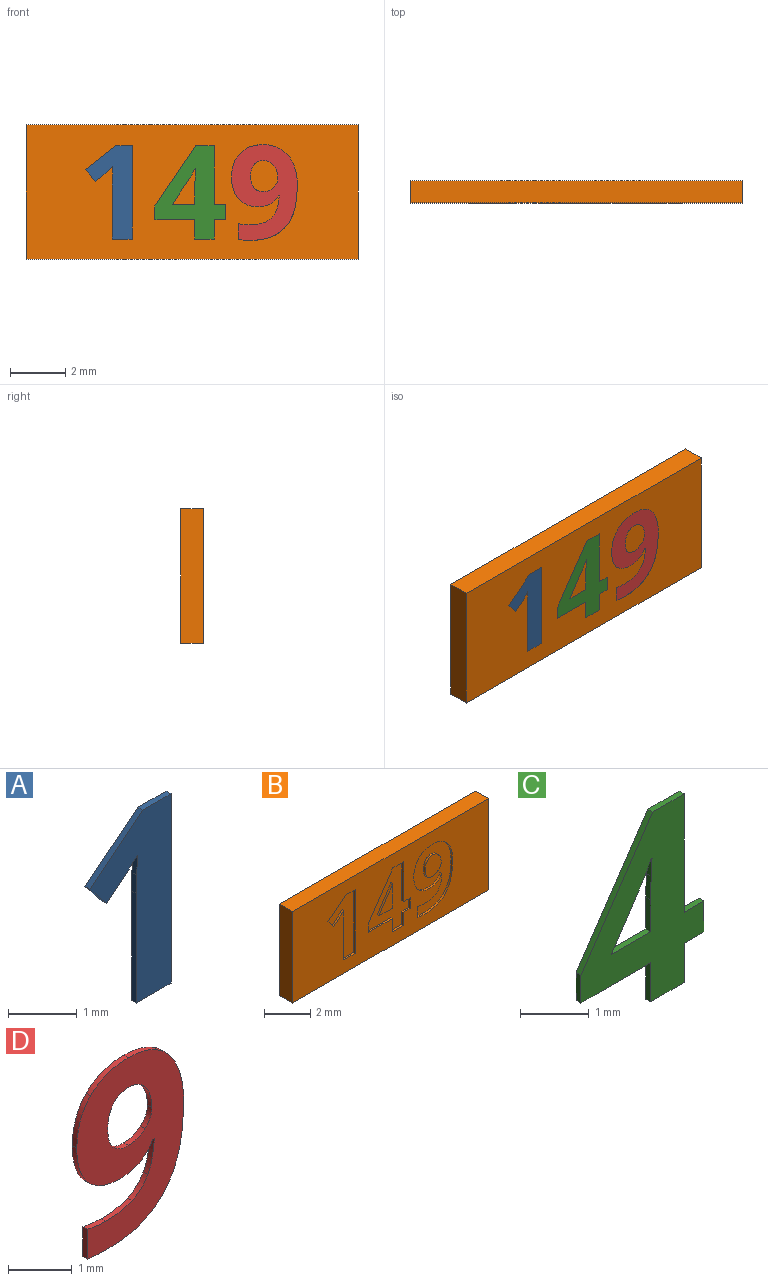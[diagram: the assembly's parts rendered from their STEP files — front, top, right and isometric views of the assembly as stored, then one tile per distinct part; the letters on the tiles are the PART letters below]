
ASSEMBLY  parts=4 mates=3
PART A: 12 faces, bbox 1.7x0.1x3.4 mm
  f0: plane 3.37x1.67mm, normal (0,-1,0), area 2.9mm2, adj f1,f2,f3,f4,f5,f6,f7,f9
  f1: plane 0.59x0.1mm, normal (0,0,1), area 0.1mm2, adj f0,f2,f8,f10
  f2: plane 1.09x0.86mm, normal (-0.62,0,0.78), area 0.1mm2, adj f0,f1,f3,f8
  f3: plane 0.43x0.34mm, normal (-0.78,0,-0.63), area 0.1mm2, adj f0,f2,f4,f8
  f4: plane 0.39x0.31mm, normal (0.63,0,-0.78), area 0mm2, adj f0,f3,f5,f8
  f5: extruded ~0.25x0.23mm, area 0mm2, adj f0,f4,f6,f8
  f6: plane 0.35x0.1mm, normal (-1,0,0.03), area 0mm2, adj f0,f5,f7,f8
  f7: plane 0.32x0.1mm, normal (-1,0,0.02), area 0mm2, adj f0,f6,f8,f9
  f8: plane 3.37x1.67mm, normal (0,1,0), area 2.9mm2, adj f1,f2,f3,f4,f5,f6,f7,f9
  f9: plane 1.95x0.1mm, normal (-1,0,0), area 0.2mm2, adj f0,f7,f8,f11
  f10: plane 3.37x0.1mm, normal (1,0,0), area 0.3mm2, adj f0,f1,f8,f11
  f11: plane 0.71x0.1mm, normal (0,0,-1), area 0.1mm2, adj f0,f8,f9,f10
PART B: 65 faces, bbox 12x0.8x4.9 mm
  f0: plane 12x4.85mm, normal (0,-1,0), area 44.7mm2, adj f1,f2,f3,f4,f6,f7,f8,f9
  f1: plane 12x0.8mm, normal (0,0,-1), area 9.6mm2, adj f0,f2,f4,f5
  f2: plane 4.85x0.8mm, normal (1,0,0), area 3.9mm2, adj f0,f1,f3,f5
  f3: plane 12x0.8mm, normal (0,0,1), area 9.6mm2, adj f0,f2,f4,f5
  f4: plane 4.85x0.8mm, normal (-1,0,0), area 3.9mm2, adj f0,f1,f3,f5
  f5: plane 12x4.85mm, normal (0,1,0), area 58.2mm2, adj f1,f2,f3,f4
  f6: extruded ~0.79x0.15mm, area 0.1mm2, adj f0,f7,f31,f32
  f7: extruded ~0.51x0.43mm, area 0.1mm2, adj f0,f6,f8,f32
  f8: extruded ~0.65x0.18mm, area 0.1mm2, adj f0,f7,f9,f32
  f9: extruded ~0.84x0.31mm, area 0.1mm2, adj f0,f8,f10,f32
  f10: extruded ~0.86x0.31mm, area 0.1mm2, adj f0,f9,f11,f32
  f11: extruded ~0.78x0.25mm, area 0.1mm2, adj f0,f10,f12,f32
  f12: extruded ~0.69x0.28mm, area 0.1mm2, adj f0,f11,f13,f32
  f13: extruded ~0.44x0.1mm, area 0mm2, adj f0,f12,f14,f32
  f14: extruded ~0.31x0.3mm, area 0mm2, adj f0,f13,f15,f32
  f15: plane 0.1x0.03mm, normal (0,0,1), area 0mm2, adj f0,f14,f16,f32
  f16: extruded ~0.62x0.14mm, area 0.1mm2, adj f0,f15,f17,f32
  f17: extruded ~0.35x0.33mm, area 0mm2, adj f0,f16,f18,f32
  f18: extruded ~0.59x0.1mm, area 0.1mm2, adj f0,f17,f19,f32
  f19: extruded ~0.41x0.1mm, area 0mm2, adj f0,f18,f20,f32
  f20: plane 0.57x0.1mm, normal (1,0,0), area 0.1mm2, adj f0,f19,f21,f32
  f21: extruded ~0.45x0.1mm, area 0mm2, adj f0,f20,f22,f32
  f22: extruded ~1.27x0.49mm, area 0.1mm2, adj f0,f21,f31,f32
  f23: extruded ~0.37x0.19mm, area 0mm2, adj f24,f30,f32,f33
  f24: extruded ~0.46x0.14mm, area 0mm2, adj f23,f25,f32,f33
  f25: extruded ~0.33x0.15mm, area 0mm2, adj f24,f26,f32,f33
  f26: extruded ~0.37x0.14mm, area 0mm2, adj f25,f27,f32,f33
  f27: extruded ~0.34x0.14mm, area 0mm2, adj f26,f28,f32,f33
  f28: extruded ~0.39x0.11mm, area 0mm2, adj f27,f29,f32,f33
  f29: extruded ~0.44x0.12mm, area 0mm2, adj f28,f30,f32,f33
  f30: extruded ~0.35x0.15mm, area 0mm2, adj f23,f29,f32,f33
  f31: extruded ~1.49x0.42mm, area 0.2mm2, adj f0,f6,f22,f32
  f32: plane 3.46x2.38mm, normal (0,-1,0), area 4.8mm2, adj f6,f7,f8,f9,f10,f11,f12,f13
  f33: plane 1.12x0.98mm, normal (0,-1,0), area 0.9mm2, adj f23,f24,f25,f26,f27,f28,f29,f30
  f34: plane 0.55x0.1mm, normal (-1,0,0), area 0.1mm2, adj f0,f35,f51,f52
  f35: plane 0.41x0.1mm, normal (0,0,-1), area 0mm2, adj f0,f34,f36,f52
  f36: plane 2.12x0.1mm, normal (-1,0,0), area 0.2mm2, adj f0,f35,f37,f52
  f37: plane 0.66x0.1mm, normal (0,0,-1), area 0.1mm2, adj f0,f36,f38,f52
  f38: plane 2.18x1.48mm, normal (0.83,0,-0.56), area 0.3mm2, adj f0,f37,f39,f52
  f39: plane 0.5x0.1mm, normal (1,0,0), area 0mm2, adj f0,f38,f40,f52
  f40: plane 1.44x0.1mm, normal (0,0,1), area 0.1mm2, adj f0,f39,f41,f52
  f41: plane 0.7x0.1mm, normal (1,0,0), area 0.1mm2, adj f0,f40,f42,f52
  f42: plane 0.7x0.1mm, normal (0,0,1), area 0.1mm2, adj f0,f41,f43,f52
  f43: plane 0.7x0.1mm, normal (-1,0,0), area 0.1mm2, adj f0,f42,f51,f52
  f44: plane 0.81x0.1mm, normal (0,0,-1), area 0.1mm2, adj f45,f50,f52,f53
  f45: plane 0.93x0.62mm, normal (-0.83,0,0.55), area 0.1mm2, adj f44,f46,f52,f53
  f46: extruded ~0.37x0.21mm, area 0mm2, adj f45,f47,f52,f53
  f47: plane 0.1x0.02mm, normal (0,0,1), area 0mm2, adj f46,f48,f52,f53
  f48: extruded ~0.32x0.1mm, area 0mm2, adj f47,f49,f52,f53
  f49: extruded ~0.42x0.1mm, area 0mm2, adj f48,f50,f52,f53
  f50: plane 0.57x0.1mm, normal (1,0,0), area 0.1mm2, adj f44,f49,f52,f53
  f51: plane 0.41x0.1mm, normal (0,0,1), area 0mm2, adj f0,f34,f43,f52
  f52: plane 3.37x2.54mm, normal (0,-1,0), area 4.3mm2, adj f34,f35,f36,f37,f38,f39,f40,f41
  f53: plane 1.3x0.84mm, normal (0,-1,0), area 0.5mm2, adj f44,f45,f46,f47,f48,f49,f50
  f54: plane 3.37x0.1mm, normal (-1,0,0), area 0.3mm2, adj f0,f55,f63,f64
  f55: plane 0.59x0.1mm, normal (0,0,-1), area 0.1mm2, adj f0,f54,f56,f64
  f56: plane 1.09x0.86mm, normal (0.62,0,-0.78), area 0.1mm2, adj f0,f55,f57,f64
  f57: plane 0.43x0.34mm, normal (0.78,0,0.63), area 0.1mm2, adj f0,f56,f58,f64
  f58: plane 0.39x0.31mm, normal (-0.63,0,0.78), area 0mm2, adj f0,f57,f59,f64
  f59: extruded ~0.25x0.23mm, area 0mm2, adj f0,f58,f60,f64
  f60: plane 0.35x0.1mm, normal (1,0,-0.03), area 0mm2, adj f0,f59,f61,f64
  f61: plane 0.32x0.1mm, normal (1,0,-0.02), area 0mm2, adj f0,f60,f62,f64
  f62: plane 1.95x0.1mm, normal (1,0,0), area 0.2mm2, adj f0,f61,f63,f64
  f63: plane 0.71x0.1mm, normal (0,0,1), area 0.1mm2, adj f0,f54,f62,f64
  f64: plane 3.37x1.67mm, normal (0,-1,0), area 2.9mm2, adj f54,f55,f56,f57,f58,f59,f60,f61
PART C: 20 faces, bbox 2.5x0.1x3.4 mm
  f0: plane 3.37x2.54mm, normal (0,-1,0), area 4.3mm2, adj f1,f2,f3,f4,f5,f6,f7,f8
  f1: plane 0.41x0.1mm, normal (0,0,1), area 0mm2, adj f0,f2,f13,f15
  f2: plane 2.12x0.1mm, normal (1,0,0), area 0.2mm2, adj f0,f1,f3,f13
  f3: plane 0.66x0.1mm, normal (0,0,1), area 0.1mm2, adj f0,f2,f4,f13
  f4: plane 2.18x1.48mm, normal (-0.83,0,0.56), area 0.3mm2, adj f0,f3,f5,f13
  f5: plane 0.5x0.1mm, normal (-1,0,0), area 0mm2, adj f0,f4,f6,f13
  f6: plane 1.44x0.1mm, normal (0,0,-1), area 0.1mm2, adj f0,f5,f7,f13
  f7: plane 0.7x0.1mm, normal (-1,0,0), area 0.1mm2, adj f0,f6,f8,f13
  f8: plane 0.7x0.1mm, normal (0,0,-1), area 0.1mm2, adj f0,f7,f13,f14
  f9: plane 0.93x0.62mm, normal (0.83,0,-0.55), area 0.1mm2, adj f0,f10,f13,f18
  f10: extruded ~0.37x0.21mm, area 0mm2, adj f0,f9,f11,f13
  f11: plane 0.1x0.02mm, normal (0,0,-1), area 0mm2, adj f0,f10,f12,f13
  f12: extruded ~0.32x0.1mm, area 0mm2, adj f0,f11,f13,f17
  f13: plane 3.37x2.54mm, normal (0,1,0), area 4.3mm2, adj f1,f2,f3,f4,f5,f6,f7,f8
  f14: plane 0.7x0.1mm, normal (1,0,0), area 0.1mm2, adj f0,f8,f13,f16
  f15: plane 0.55x0.1mm, normal (1,0,0), area 0.1mm2, adj f0,f1,f13,f16
  f16: plane 0.41x0.1mm, normal (0,0,-1), area 0mm2, adj f0,f13,f14,f15
  f17: extruded ~0.42x0.1mm, area 0mm2, adj f0,f12,f13,f19
  f18: plane 0.81x0.1mm, normal (0,0,1), area 0.1mm2, adj f0,f9,f13,f19
  f19: plane 0.57x0.1mm, normal (-1,0,0), area 0.1mm2, adj f0,f13,f17,f18
PART D: 28 faces, bbox 2.4x0.1x3.5 mm
  f0: plane 3.46x2.38mm, normal (0,-1,0), area 4.8mm2, adj f1,f2,f3,f4,f5,f6,f7,f8
  f1: extruded ~0.51x0.43mm, area 0.1mm2, adj f0,f2,f21,f23
  f2: extruded ~0.65x0.18mm, area 0.1mm2, adj f0,f1,f3,f21
  f3: extruded ~0.84x0.31mm, area 0.1mm2, adj f0,f2,f4,f21
  f4: extruded ~0.86x0.31mm, area 0.1mm2, adj f0,f3,f5,f21
  f5: extruded ~0.78x0.25mm, area 0.1mm2, adj f0,f4,f6,f21
  f6: extruded ~0.69x0.28mm, area 0.1mm2, adj f0,f5,f7,f21
  f7: extruded ~0.44x0.1mm, area 0mm2, adj f0,f6,f8,f21
  f8: extruded ~0.31x0.3mm, area 0mm2, adj f0,f7,f9,f21
  f9: plane 0.1x0.03mm, normal (0,0,-1), area 0mm2, adj f0,f8,f10,f21
  f10: extruded ~0.62x0.14mm, area 0.1mm2, adj f0,f9,f11,f21
  f11: extruded ~0.35x0.33mm, area 0mm2, adj f0,f10,f12,f21
  f12: extruded ~0.59x0.1mm, area 0.1mm2, adj f0,f11,f13,f21
  f13: extruded ~0.41x0.1mm, area 0mm2, adj f0,f12,f14,f21
  f14: plane 0.57x0.1mm, normal (-1,0,0), area 0.1mm2, adj f0,f13,f15,f21
  f15: extruded ~0.45x0.1mm, area 0mm2, adj f0,f14,f21,f22
  f16: extruded ~0.46x0.14mm, area 0mm2, adj f0,f17,f21,f26
  f17: extruded ~0.33x0.15mm, area 0mm2, adj f0,f16,f18,f21
  f18: extruded ~0.37x0.14mm, area 0mm2, adj f0,f17,f19,f21
  f19: extruded ~0.34x0.14mm, area 0mm2, adj f0,f18,f20,f21
  f20: extruded ~0.39x0.11mm, area 0mm2, adj f0,f19,f21,f25
  f21: plane 3.46x2.38mm, normal (0,1,0), area 4.8mm2, adj f1,f2,f3,f4,f5,f6,f7,f8
  f22: extruded ~1.27x0.49mm, area 0.1mm2, adj f0,f15,f21,f24
  f23: extruded ~0.79x0.15mm, area 0.1mm2, adj f0,f1,f21,f24
  f24: extruded ~1.49x0.42mm, area 0.2mm2, adj f0,f21,f22,f23
  f25: extruded ~0.44x0.12mm, area 0mm2, adj f0,f20,f21,f27
  f26: extruded ~0.37x0.19mm, area 0mm2, adj f0,f16,f21,f27
  f27: extruded ~0.35x0.15mm, area 0mm2, adj f0,f21,f25,f26
PLACE A t=(-4.57,0.39,0)mm
PLACE B t=(-0.01,0.39,0)mm
PLACE C t=(-1.54,0.39,0)mm
PLACE D t=(1.11,0.39,0)mm
MATE fastened A.f0 <-> B.f0  axis (0,-1,0) through (-2.89,-0.41,-1.7)mm
MATE fastened C.f0 <-> B.f0  axis (0,-1,0) through (0.09,-0.41,-1.7)mm
MATE fastened D.f0 <-> B.f0  axis (0,-1,0) through (1.65,-0.41,-1.72)mm
